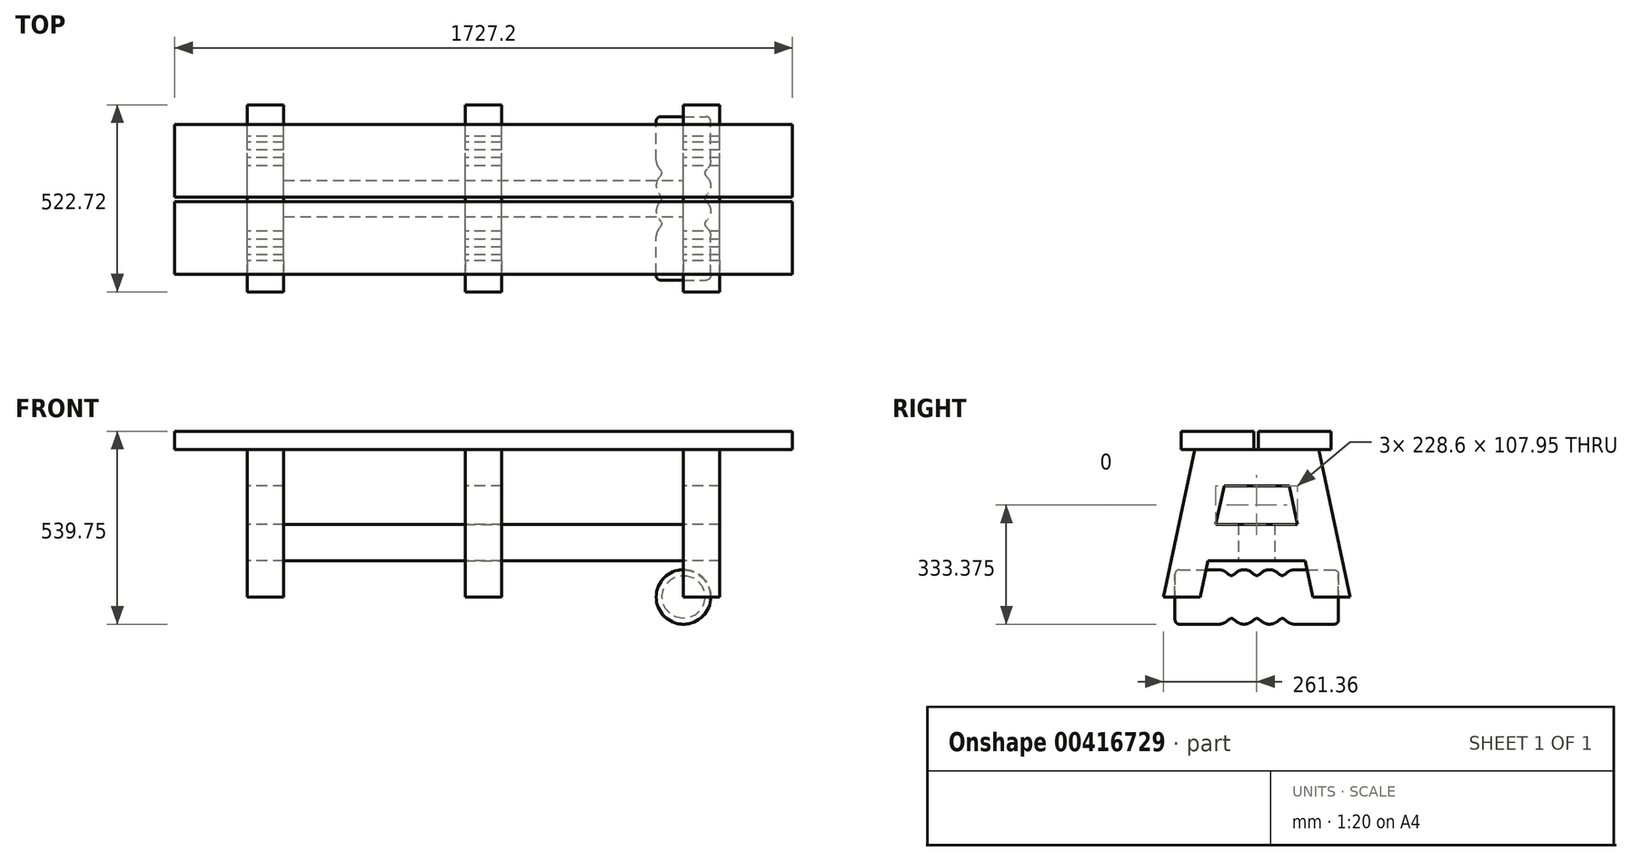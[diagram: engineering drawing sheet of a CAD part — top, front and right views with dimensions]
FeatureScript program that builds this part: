
annotation { "Feature Type Name" : "Feature", "Feature Type Description" : "" }
export const myFeature = defineFeature(function(context is Context, id is Id, definition is map)
    precondition{}
    {
        {
            var Q0;
            Q0=qCreatedBy(makeId("Top.planeOp"),FACE);
            var sketch = newSketch(context, id + "F0", { "sketchPlane" : qUnion([Q0])});
            skLineSegment(sketch, "E0", {"start": v(0, 457.2) * mm, "end": v(0, -457.2) * mm});
            skCircle(sketch, "E1", {"center": v(41.91, 35.56) * mm, "radius": 34.3 * mm});
            skCircle(sketch, "E2", {"center": v(41.91, -35.56) * mm, "radius": 34.3 * mm});
            skLineSegment(sketch, "E3", {"start": v(41.91, 35.56) * mm, "end": v(41.91, -35.56) * mm});
            skLineSegment(sketch, "E4", {"start": v(0, 0) * mm, "end": v(41.91, 0) * mm});
            skFitSpline(sketch, "E5", {"points": [v(68.48, 13.88) * mm, v(68.48, -13.88) * mm], "startDerivative": vector(-33.98, -41.64) * mm, "endDerivative": vector(33.98, -41.64) * mm});
            skLineSegment(sketch, "E6", {"start": v(41.91, 0) * mm, "end": v(57.15, 0) * mm});
            skLineSegment(sketch, "E7", {"start": v(76.2, 35.56) * mm, "end": v(76.2, 228.6) * mm});
            skLineSegment(sketch, "E8", {"start": v(76.2, -35.56) * mm, "end": v(76.2, -228.6) * mm});
            skCircle(sketch, "E9", {"center": v(41.91, -106.68) * mm, "radius": 34.3 * mm});
            skCircle(sketch, "E10", {"center": v(41.91, 106.68) * mm, "radius": 34.3 * mm});
            skLineSegment(sketch, "E11", {"start": v(0, -71.12) * mm, "end": v(57.15, -71.12) * mm});
            skLineSegment(sketch, "E12", {"start": v(0, 71.12) * mm, "end": v(57.15, 71.12) * mm});
            skFitSpline(sketch, "E13", {"points": [v(68.48, -57.24) * mm, v(68.48, -85) * mm], "startDerivative": vector(-33.98, -41.64) * mm, "endDerivative": vector(33.98, -41.64) * mm});
            skFitSpline(sketch, "E14", {"points": [v(68.48, 85) * mm, v(68.48, 57.24) * mm], "startDerivative": vector(-33.98, -41.64) * mm, "endDerivative": vector(33.98, -41.64) * mm});
            skLineSegment(sketch, "E15", {"start": v(76.2, -228.6) * mm, "end": v(0, -228.6) * mm});
            skLineSegment(sketch, "E16", {"start": v(76.2, 228.6) * mm, "end": v(0, 228.6) * mm});
            skSolve(sketch);
        }
        {
            var Q0;
            {var subQ0=sQuery(id+"F0.wireOp",EDGE,"E4");Q0=makeQuery(id+"F0.imprint","IMPRINT",FACE,{"disambiguationData":[TD([[makeQuery(id+"F0.imprint","IMPRINT",EDGE,{"derivedFrom":subQ0}),1.0]])]});}
            var Q1;
            {var subQ0=sQuery(id+"F0.wireOp",EDGE,"E10");var subQ1=makeQuery(id+"F0.imprint","INTERSECT",VERTEX,{"derivedFrom":[subQ0,sQuery(id+"F0.wireOp",EDGE,"E14")]});Q1=makeQuery(id+"F0.imprint","IMPRINT",FACE,{"disambiguationData":[TD([[makeQuery(id+"F0.imprint","IMPRINT",EDGE,{"disambiguationData":[TD([[subQ1,1.0]])],"derivedFrom":subQ0}),1.0]])]});}
            var Q2;
            {var subQ0=sQuery(id+"F0.wireOp",EDGE,"E1");var subQ1=makeQuery(id+"F0.imprint","INTERSECT",VERTEX,{"derivedFrom":[subQ0,sQuery(id+"F0.wireOp",EDGE,"E7")]});Q2=makeQuery(id+"F0.imprint","IMPRINT",FACE,{"disambiguationData":[TD([[makeQuery(id+"F0.imprint","IMPRINT",EDGE,{"disambiguationData":[TD([[subQ1,-1.0]])],"derivedFrom":subQ0}),1.0]])]});}
            var Q3;
            {var subQ0=sQuery(id+"F0.wireOp",EDGE,"E2");var subQ1=makeQuery(id+"F0.imprint","INTERSECT",VERTEX,{"derivedFrom":[subQ0,sQuery(id+"F0.wireOp",EDGE,"E5")]});Q3=makeQuery(id+"F0.imprint","IMPRINT",FACE,{"disambiguationData":[TD([[makeQuery(id+"F0.imprint","IMPRINT",EDGE,{"disambiguationData":[TD([[subQ1,1.0]])],"derivedFrom":subQ0}),1.0]])]});}
            var Q4;
            {var subQ6=sQuery(id+"F0.wireOp",EDGE,"E5");Q4=makeQuery(id+"F0.imprint","IMPRINT",FACE,{"disambiguationData":[TD([[makeQuery(id+"F0.imprint","IMPRINT",EDGE,{"derivedFrom":subQ6}),-1.0]])]});}
            var Q5;
            {var subQ7=sQuery(id+"F0.wireOp",EDGE,"E4");Q5=makeQuery(id+"F0.imprint","IMPRINT",FACE,{"disambiguationData":[TD([[makeQuery(id+"F0.imprint","IMPRINT",EDGE,{"derivedFrom":subQ7}),-1.0]])]});}
            var Q6;
            {var subQ0=sQuery(id+"F0.wireOp",EDGE,"E9");var subQ1=makeQuery(id+"F0.imprint","INTERSECT",VERTEX,{"derivedFrom":[subQ0,sQuery(id+"F0.wireOp",EDGE,"E13")]});Q6=makeQuery(id+"F0.imprint","IMPRINT",FACE,{"disambiguationData":[TD([[makeQuery(id+"F0.imprint","IMPRINT",EDGE,{"disambiguationData":[TD([[subQ1,1.0]])],"derivedFrom":subQ0}),1.0]])]});}
            var Q7;
            Q7=sQuery(id+"F0.wireOp",EDGE,"E0");
            revolve(context, id + "F1", {"entities" : qUnion([Q0, Q1, Q2, Q3, Q4, Q5, Q6]), "axis" : qUnion([Q7]), "revolveType" : RevolveType.FULL});
        }
        {
            var Q0;
            Q0=makeQuery(id+"F1.opRevolve","SWEPT_EDGE",EDGE,{"disambiguationData":[OSD([sQuery(id+"F0.wireOp",EDGE,"E7"),sQuery(id+"F0.wireOp",EDGE,"E16")])]});
            var Q1;
            Q1=makeQuery(id+"F1.opRevolve","SWEPT_EDGE",EDGE,{"disambiguationData":[OSD([sQuery(id+"F0.wireOp",EDGE,"E8"),sQuery(id+"F0.wireOp",EDGE,"E15")])]});
            fillet(context, id + "F2", {"entities" : qUnion([Q0, Q1]), "radius" : 12.7 * mm, "tangentPropagation" : true, "allowEdgeOverflow" : false});
        }
        {
            var Q0;
            Q0=qCreatedBy(makeId("Right.planeOp"),FACE);
            var sketch = newSketch(context, id + "F3", { "sketchPlane" : qUnion([Q0])});
            skLineSegment(sketch, "E17", {"start": v(-173.63, 412.75) * mm, "end": v(-261.36, 0) * mm});
            skLineSegment(sketch, "E18", {"start": v(-173.63, 412.75) * mm, "end": v(173.63, 412.75) * mm});
            skLineSegment(sketch, "E19", {"start": v(173.63, 412.75) * mm, "end": v(261.36, 0) * mm});
            skLineSegment(sketch, "E20", {"start": v(0, 412.75) * mm, "end": v(0, 0) * mm, "construction": true});
            skLineSegment(sketch, "E21", {"start": v(-261.36, 0) * mm, "end": v(-157.5, 0) * mm});
            skLineSegment(sketch, "E22", {"start": v(-157.5, 0) * mm, "end": v(-91.35, 311.15) * mm});
            skLineSegment(sketch, "E23", {"start": v(-91.35, 311.15) * mm, "end": v(91.35, 311.15) * mm});
            skLineSegment(sketch, "E24", {"start": v(91.35, 311.15) * mm, "end": v(157.5, 0) * mm});
            skLineSegment(sketch, "E25", {"start": v(157.5, 0) * mm, "end": v(261.36, 0) * mm});
            skLineSegment(sketch, "E26", {"start": v(91.35, 311.15) * mm, "end": v(69.76, 412.75) * mm});
            skLineSegment(sketch, "E27", {"start": v(-91.35, 311.15) * mm, "end": v(-69.76, 412.75) * mm});
            skLineSegment(sketch, "E28", {"start": v(-114.3, 203.2) * mm, "end": v(114.3, 203.2) * mm});
            skLineSegment(sketch, "E29", {"start": v(-135.9, 101.6) * mm, "end": v(135.9, 101.6) * mm});
            skSolve(sketch);
        }
        {
            var Q0;
            Q0=makeQuery(id+"F3.imprint","IMPRINT",FACE,{"disambiguationData":[TD([[makeQuery(id+"F3.imprint","IMPRINT",EDGE,{"derivedFrom":sQuery(id+"F3.wireOp",EDGE,"E23")}),1.0]])]});
            var Q1;
            {var subQ4=sQuery(id+"F3.wireOp",EDGE,"E17");Q1=makeQuery(id+"F3.imprint","IMPRINT",FACE,{"disambiguationData":[TD([[makeQuery(id+"F3.imprint","IMPRINT",EDGE,{"derivedFrom":subQ4}),1.0]])]});}
            var Q2;
            {var subQ0=sQuery(id+"F3.wireOp",EDGE,"E28");Q2=makeQuery(id+"F3.imprint","IMPRINT",FACE,{"disambiguationData":[TD([[makeQuery(id+"F3.imprint","IMPRINT",EDGE,{"derivedFrom":subQ0}),-1.0]])]});}
            var Q3;
            {var subQ4=sQuery(id+"F3.wireOp",EDGE,"E19");Q3=makeQuery(id+"F3.imprint","IMPRINT",FACE,{"disambiguationData":[TD([[makeQuery(id+"F3.imprint","IMPRINT",EDGE,{"derivedFrom":subQ4}),-1.0]])]});}
            extrude(context, id + "F4", {"entities" : qUnion([Q0, Q1, Q2, Q3]), "depth" : 101.6 * mm, "offsetDistance" : 25.4 * mm});
        }
        {
            var Q0;
            Q0=qCreatedBy(makeId("Right.planeOp"),FACE);
            var sketch = newSketch(context, id + "F5", { "sketchPlane" : qUnion([Q0])});
            skLineSegment(sketch, "E30", {"start": v(0, 0) * mm, "end": v(0, 834.82) * mm, "construction": true});
            skLineSegment(sketch, "E31.0", {"start": v(-173.63, 412.75) * mm, "end": v(173.63, 412.75) * mm});
            skLineSegment(sketch, "E32.0", {"start": v(-114.3, 203.2) * mm, "end": v(114.3, 203.2) * mm});
            skLineSegment(sketch, "E33.0", {"start": v(-135.9, 101.6) * mm, "end": v(135.9, 101.6) * mm});
            skLineSegment(sketch, "E34.0", {"start": v(-91.35, 311.15) * mm, "end": v(91.35, 311.15) * mm});
            skLineSegment(sketch, "E35", {"start": v(-50.8, 203.2) * mm, "end": v(-50.8, 101.6) * mm});
            skLineSegment(sketch, "E36", {"start": v(50.8, 203.2) * mm, "end": v(50.8, 101.6) * mm});
            skLineSegment(sketch, "E37.bottom", {"start": v(-91.35, 311.15) * mm, "end": v(-40.55, 311.15) * mm});
            skLineSegment(sketch, "E37.top", {"start": v(-91.35, 412.75) * mm, "end": v(-40.55, 412.75) * mm});
            skLineSegment(sketch, "E37.left", {"start": v(-91.35, 311.15) * mm, "end": v(-91.35, 412.75) * mm});
            skLineSegment(sketch, "E37.right", {"start": v(-40.55, 311.15) * mm, "end": v(-40.55, 412.75) * mm});
            skLineSegment(sketch, "E38.bottom", {"start": v(91.35, 311.15) * mm, "end": v(40.55, 311.15) * mm});
            skLineSegment(sketch, "E38.top", {"start": v(91.35, 412.75) * mm, "end": v(40.55, 412.75) * mm});
            skLineSegment(sketch, "E38.left", {"start": v(91.35, 311.15) * mm, "end": v(91.35, 412.75) * mm});
            skLineSegment(sketch, "E38.right", {"start": v(40.55, 311.15) * mm, "end": v(40.55, 412.75) * mm});
            skSolve(sketch);
        }
        {
            var Q0;
            Q0=makeQuery(id+"F5.imprint","IMPRINT",FACE,{"disambiguationData":[TD([[makeQuery(id+"F5.imprint","IMPRINT",EDGE,{"derivedFrom":sQuery(id+"F5.wireOp",EDGE,"E38.bottom")}),-1.0]])]});
            var Q1;
            Q1=makeQuery(id+"F5.imprint","IMPRINT",FACE,{"disambiguationData":[TD([[makeQuery(id+"F5.imprint","IMPRINT",EDGE,{"derivedFrom":sQuery(id+"F5.wireOp",EDGE,"E37.bottom")}),1.0]])]});
            var Q2;
            {var subQ0=sQuery(id+"F5.wireOp",EDGE,"E35");Q2=makeQuery(id+"F5.imprint","IMPRINT",FACE,{"disambiguationData":[TD([[makeQuery(id+"F5.imprint","IMPRINT",EDGE,{"derivedFrom":subQ0}),1.0]])]});}
            extrude(context, id + "F6", {"entities" : qUnion([Q0, Q1, Q2]), "oppositeDirection" : true, "depth" : 1117.6 * mm, "offsetDistance" : 25.4 * mm});
        }
        {
            var Q0;
            Q0=makeQuery(id+"F4.opExtrude","SWEPT_BODY",BODY,{"disambiguationData":[OSD([sQuery(id+"F3.wireOp",EDGE,"E17"),sQuery(id+"F3.wireOp",EDGE,"E18"),sQuery(id+"F3.wireOp",EDGE,"E19"),sQuery(id+"F3.wireOp",EDGE,"E21"),sQuery(id+"F3.wireOp",EDGE,"E22"),sQuery(id+"F3.wireOp",EDGE,"E23"),sQuery(id+"F3.wireOp",EDGE,"E24"),sQuery(id+"F3.wireOp",EDGE,"E25"),sQuery(id+"F3.wireOp",EDGE,"E28"),sQuery(id+"F3.wireOp",EDGE,"E29")])]});
            transform(context, id + "F7", {"entities" : qUnion([Q0]), "transformType" : TransformType.TRANSLATION_3D, "dx" : -1219.2 * mm, "dy" : 0 * mm, "dz" : 0 * mm, "makeCopy" : true});
        }
        {
            var Q0;
            Q0=qCreatedBy(makeId("Right.planeOp"),FACE);
            var sketch = newSketch(context, id + "F8", { "sketchPlane" : qUnion([Q0])});
            skLineSegment(sketch, "E39.0", {"start": v(-173.63, 412.75) * mm, "end": v(173.63, 412.75) * mm, "construction": true});
            skLineSegment(sketch, "E40.bottom", {"start": v(-8.53, 412.75) * mm, "end": v(-211.73, 412.75) * mm});
            skLineSegment(sketch, "E40.top", {"start": v(-8.53, 463.55) * mm, "end": v(-211.73, 463.55) * mm});
            skLineSegment(sketch, "E40.left", {"start": v(-8.53, 412.75) * mm, "end": v(-8.53, 463.55) * mm});
            skLineSegment(sketch, "E40.right", {"start": v(-211.73, 412.75) * mm, "end": v(-211.73, 463.55) * mm});
            skLineSegment(sketch, "E41.bottom", {"start": v(4.17, 412.75) * mm, "end": v(207.37, 412.75) * mm});
            skLineSegment(sketch, "E41.top", {"start": v(4.17, 463.55) * mm, "end": v(207.37, 463.55) * mm});
            skLineSegment(sketch, "E41.left", {"start": v(4.17, 412.75) * mm, "end": v(4.17, 463.55) * mm});
            skLineSegment(sketch, "E41.right", {"start": v(207.37, 412.75) * mm, "end": v(207.37, 463.55) * mm});
            skLineSegment(sketch, "E42.bottom", {"start": v(220.07, 412.75) * mm, "end": v(423.27, 412.75) * mm});
            skLineSegment(sketch, "E42.top", {"start": v(220.07, 463.55) * mm, "end": v(423.27, 463.55) * mm});
            skLineSegment(sketch, "E42.left", {"start": v(220.07, 412.75) * mm, "end": v(220.07, 463.55) * mm});
            skLineSegment(sketch, "E42.right", {"start": v(423.27, 412.75) * mm, "end": v(423.27, 463.55) * mm});
            skSolve(sketch);
        }
        {
            var Q0;
            Q0=makeQuery(id+"F8.imprint","IMPRINT",FACE,{"disambiguationData":[TD([[makeQuery(id+"F8.imprint","IMPRINT",EDGE,{"derivedFrom":sQuery(id+"F8.wireOp",EDGE,"E40.bottom")}),-1.0]])]});
            var Q1;
            Q1=makeQuery(id+"F8.imprint","IMPRINT",FACE,{"disambiguationData":[TD([[makeQuery(id+"F8.imprint","IMPRINT",EDGE,{"derivedFrom":sQuery(id+"F8.wireOp",EDGE,"E41.bottom")}),1.0]])]});
            extrude(context, id + "F9", {"entities" : qUnion([Q0, Q1]), "depth" : 304.8 * mm, "offsetDistance" : 25.4 * mm, "hasSecondDirection" : true, "secondDirectionOppositeDirection" : true, "secondDirectionDepth" : 1422.4 * mm});
        }
        {
            var Q0;
            Q0=makeQuery(id+"F4.opExtrude","SWEPT_BODY",BODY,{"disambiguationData":[OSD([sQuery(id+"F3.wireOp",EDGE,"E17"),sQuery(id+"F3.wireOp",EDGE,"E18"),sQuery(id+"F3.wireOp",EDGE,"E19"),sQuery(id+"F3.wireOp",EDGE,"E21"),sQuery(id+"F3.wireOp",EDGE,"E22"),sQuery(id+"F3.wireOp",EDGE,"E23"),sQuery(id+"F3.wireOp",EDGE,"E24"),sQuery(id+"F3.wireOp",EDGE,"E25"),sQuery(id+"F3.wireOp",EDGE,"E28"),sQuery(id+"F3.wireOp",EDGE,"E29")])]});
            transform(context, id + "F10", {"entities" : qUnion([Q0]), "transformType" : TransformType.TRANSLATION_3D, "dx" : -609.6 * mm, "dy" : 0 * mm, "dz" : 0 * mm, "makeCopy" : true});
        }
    });
